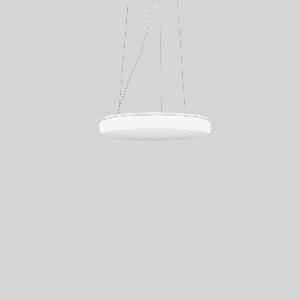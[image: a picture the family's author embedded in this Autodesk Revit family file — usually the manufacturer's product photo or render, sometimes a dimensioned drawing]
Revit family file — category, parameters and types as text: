
# Revit family: flat_polymero_kreis_slim_312090_002_1_76_7fa8
name_source: partatom
category: Lighting Fixtures
units: mm (PartAtom-declared; Revit-internal decimal feet)

## family parameters
Cut with Voids When Loaded = No
Host = Face
Light Source = No
Part Type = Normal
Room Calculation Point = No
Round Connector Dimension = Use Diameter
Shared = No

## types (1)
- FLAT POLYMERO KREIS SLIM (1 x LED Modul 830, 1900 lm, 3000)
    Apparent Load = 19 VA
    CIE Flux Codes = 43 74 93 88 100
    Color Rendering = 80
    Color Temperature = 3000
    Default Elevation = 1800 mm
    Description = Series: FLAT POLYMERO KREIS SLIM
Decorative round LED pendant luminaire. Base and canopy: metal, powder-coated, white. Canopy Ø 205 mm, h 35 mm. Diffuser made of non-yellowing plastic (PMMA), opal. Diffuser fastening: patented push system. Homogeneous and smooth light distribution. Suitable for pendant. 3-point steel cable suspension, steplessly adjustable. Special lengths available on request. TouchDim sensor capable. Light and/or presence sensors can be integrated. 
Colour: white
Diameter: 460 mm
Height: 68 mm
Suspension length: 200-1300 mm
Lamp: LED
Socket: without socket
Colour temperature: 3000K
Colour rendering index (CRI): 83
System power: 19 W
Rated luminous flux: 1900 lm
Luminous efficiency: 100 lm/W
Control gear: AC power, DALI dimmable
Protection class: I
Type of protection: IP 40
    Height = 68 mm
    Lamp = 1 x LED Modul 830
    Lamp Light Flux = 1900 lm
    Lamp count = 1
    Length = 460 mm
    Lifetime = 50000 h
    Luminous efficacy = 100 lm/W
    Manufacturer = RZB
    ModVariant = No
    Model = 312090.002.1.76
    Mounting Place = Ceiling
    Mounting Type = Pendant
    Number of Poles = 1
    OnlyDefault = Yes
    Power Factor = 1
    Product Name = FLAT POLYMERO KREIS SLIM
    Product group = Pendant luminaires
    ProductGroupID = 902
    Protection Class = Protection class I
    Protection Degree = IP 40
    RLX_Detail_Level = 1
    RLX_Emergency_Light_Flux = 0 lm
    RLX_Emergency_Type = 0
    RLX_Emergency_Type_DB = No
    RlxData = <blob elided: 57669 chars, md5=651590e5>
    Socket = socket
    Standby Power = 0 W
    System Light Flux = 1900 lm
    System Power = 19 W
    Type Comments = Product without accessories
    Type Image = 312090.002.jpg
    URL = http://relux.com
    VarID = ---
    Voltage = 230 V
    Voltage Range = 220-240 V
    Weight = 0.00 kg
    Width = 0 mm  [stored 0 ft]

note: [stored X ft] marks values corroborated as IEEE doubles in the binary element streams (Revit-internal decimal feet)

## geometry (parser evidence)
native form markers: Blend x4, Sweep x14
no freeform markers — native parametric forms only
